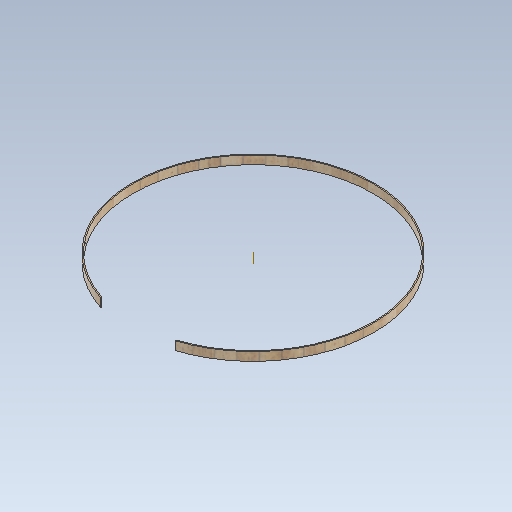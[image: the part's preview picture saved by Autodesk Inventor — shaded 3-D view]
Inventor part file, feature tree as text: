
AUTODESK INVENTOR PART (.ipt)
format: ipt  version: 2020 (Build 240168000, 168)  size: 215,552 bytes
history: native  units: mm
features: extrude x2, sketch x1
ambient origin geometry x8: Origin, YZ Plane, XZ Plane, XY Plane, X Axis, Y Axis, Z Axis, Center Point
bodies: Body1 (feature_tree)
feature tree (3):
  extrude  "Extrusion3"  Depth=10.0mm
  sketch  "Sketch3"  dims[d15=30.0mm d16=0.0mm d40=3.25mm d52=4.363323mm d60=0.872665mm d61=12.566371mm d62=13.439035mm d84=858.0mm d85=850.0mm d87=150.07mm d88=429.0mm d89=4.363323mm d90=1.919862mm d91=1.919862mm d157=10.0mm d158=0.0mm d174=0.5mm d175=0.872665mm d176=0.5mm d177=0.872665mm]
  extrude  "Extrusion10"  Depth=10.0mm
